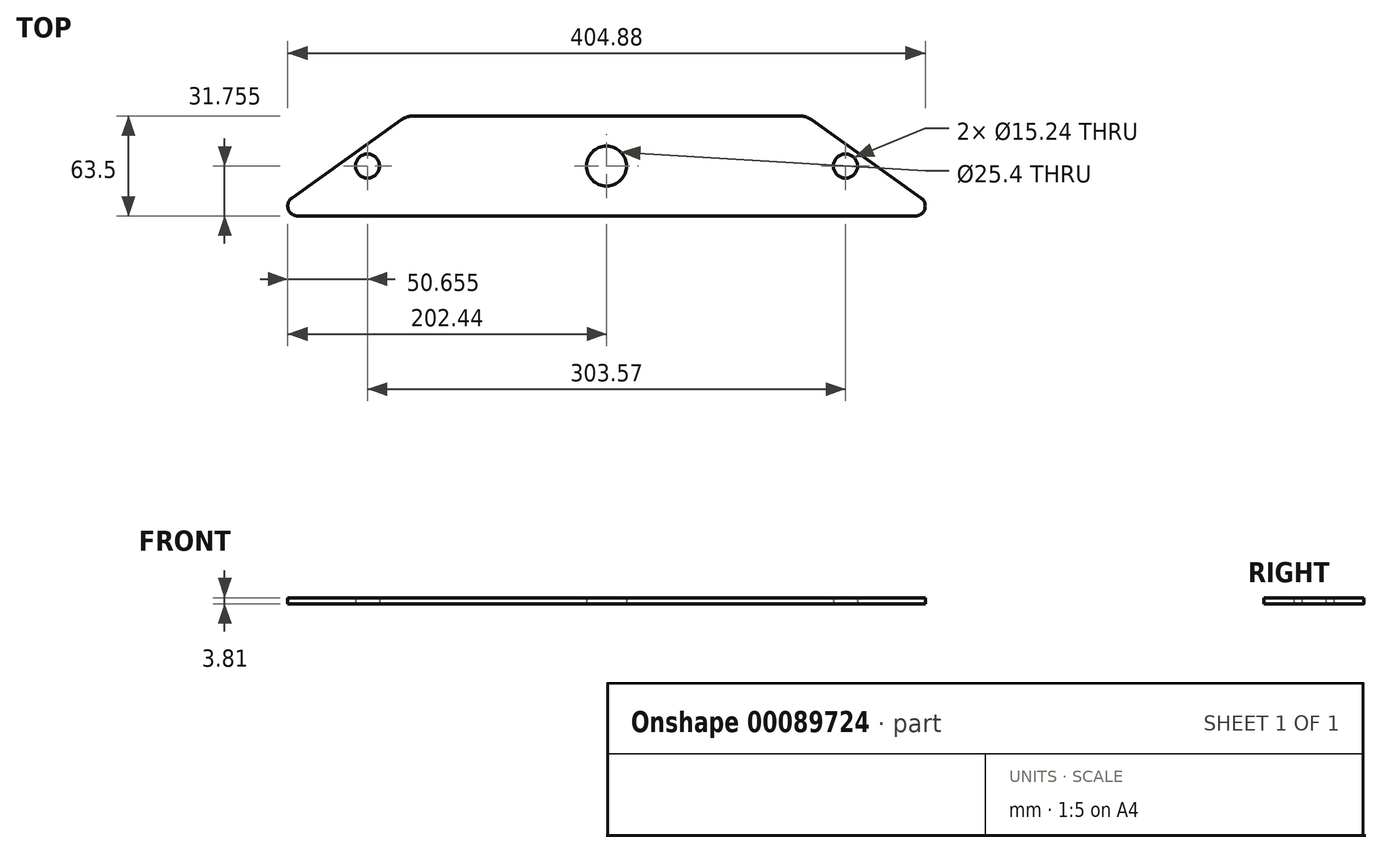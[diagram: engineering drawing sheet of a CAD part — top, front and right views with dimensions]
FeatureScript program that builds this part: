
annotation { "Feature Type Name" : "Feature", "Feature Type Description" : "" }
export const myFeature = defineFeature(function(context is Context, id is Id, definition is map)
    precondition{}
    {
        {
            var Q0;
            Q0=qCreatedBy(makeId("Top.planeOp"),FACE);
            var sketch = newSketch(context, id + "F0", { "sketchPlane" : qUnion([Q0])});
            skLineSegment(sketch, "E0", {"start": v(0, -13.52) * mm, "end": v(-196.09, -13.52) * mm});
            skLineSegment(sketch, "E1", {"start": v(0, 49.98) * mm, "end": v(-122.93, 49.98) * mm});
            skLineSegment(sketch, "E2.MirrorCS", {"start": v(0, -13.52) * mm, "end": v(196.09, -13.52) * mm});
            skLineSegment(sketch, "E3.MirrorCS", {"start": v(0, 49.98) * mm, "end": v(122.93, 49.98) * mm});
            skLineSegment(sketch, "E4", {"start": v(-199.78, -2) * mm, "end": v(-130.31, 47.62) * mm});
            skLineSegment(sketch, "E5", {"start": v(130.31, 47.62) * mm, "end": v(199.78, -2) * mm});
            skPoint(sketch, "E6.visualSharp", {"position": v(-127, 49.98) * mm});
            skArc(sketch, "E6.filletArc", {"start": v(-122.93, 49.98) * mm, "mid": v(-126.8, 49.38) * mm, "end": v(-130.31, 47.62) * mm});
            skPoint(sketch, "E7.visualSharp", {"position": v(127, 49.98) * mm});
            skArc(sketch, "E7.filletArc", {"start": v(130.31, 47.62) * mm, "mid": v(126.8, 49.38) * mm, "end": v(122.93, 49.98) * mm});
            skPoint(sketch, "E8.visualSharp", {"position": v(-215.9, -13.52) * mm});
            skArc(sketch, "E8.filletArc", {"start": v(-199.78, -2) * mm, "mid": v(-202.13, -9.1) * mm, "end": v(-196.09, -13.52) * mm});
            skPoint(sketch, "E9.visualSharp", {"position": v(215.9, -13.52) * mm});
            skArc(sketch, "E9.filletArc", {"start": v(196.09, -13.52) * mm, "mid": v(202.13, -9.1) * mm, "end": v(199.78, -2) * mm});
            skCircle(sketch, "E10", {"center": v(0, 18.23) * mm, "radius": 12.7 * mm});
            skCircle(sketch, "E11", {"center": v(-151.79, 18.23) * mm, "radius": 7.62 * mm});
            skCircle(sketch, "E12.MirrorC", {"center": v(151.79, 18.23) * mm, "radius": 7.62 * mm});
            skSolve(sketch);
        }
        {
            var Q0;
            Q0=makeQuery(id+"F0.imprint","IMPRINT",FACE,{"disambiguationData":[TD([[makeQuery(id+"F0.imprint","IMPRINT",EDGE,{"derivedFrom":sQuery(id+"F0.wireOp",EDGE,"E0")}),-1.0]])]});
            extrude(context, id + "F1", {"entities" : qUnion([Q0]), "depth" : 3.8 * mm});
        }
    });
